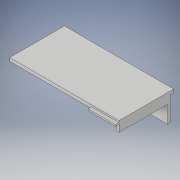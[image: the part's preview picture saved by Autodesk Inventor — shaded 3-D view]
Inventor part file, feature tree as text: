
AUTODESK INVENTOR PART (.ipt)
format: ipt  version: 2019 (Build 230136000, 136)  size: 128,000 bytes
history: native  units: in
note: dims shown in document units (in); Inventor stores cm internally (conversion verified against a paired STEP export)
features: extrude x4, sketch x4
ambient origin geometry x8: Origin, YZ Plane, XZ Plane, XY Plane, X Axis, Y Axis, Z Axis, Center Point
bodies: Solid1 (feature_tree)
feature tree (8):
  extrude  "Extrusion1"  Depth=2.0in
  extrude  "Extrusion3"  Depth=0.13in
  extrude  "Extrusion4"  Depth=0.1in
  extrude  "Extrusion5"  Depth=0.1in
  sketch  "Sketch1"  dims[d0=4.0in d1=2.0in]
  sketch  "Sketch3"  dims[d2=0.125in d3=0.0in d8=0.13in]
  sketch  "Sketch4"  dims[d9=0.13in d10=0.1in]
  sketch  "Sketch5"  dims[d11=1.0in d12=0.0in d13=0.1in d14=0.375in d15=0.0in d16=1.0in d17=0.06in d18=0.125in d19=0.0in]
